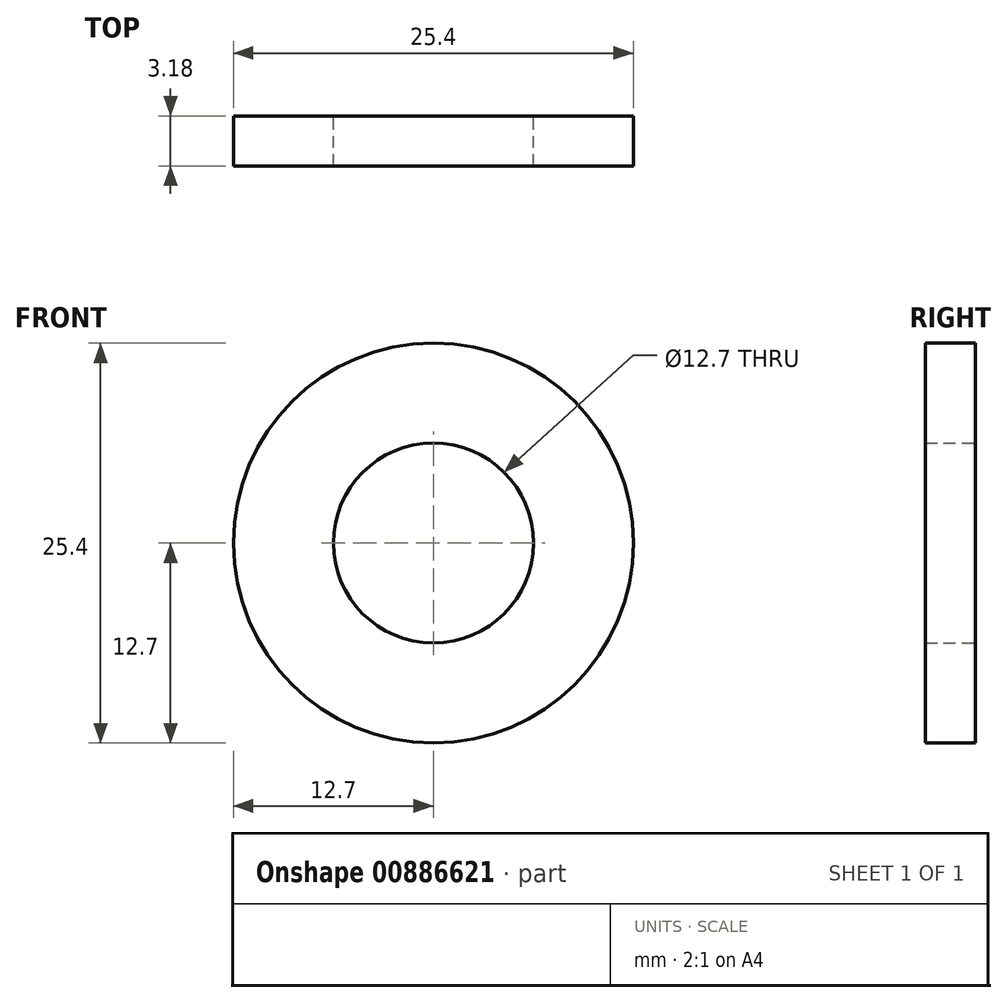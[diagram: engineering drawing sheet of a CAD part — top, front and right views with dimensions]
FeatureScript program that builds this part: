
annotation { "Feature Type Name" : "Feature", "Feature Type Description" : "" }
export const myFeature = defineFeature(function(context is Context, id is Id, definition is map)
    precondition{}
    {
        {
            assignVariable(context, id + "F0", {"name" : "thickness", "anyValue" : 3.17 * mm});
        }
        {
            var Q0;
            Q0=qCreatedBy(makeId("Front.planeOp"),FACE);
            var sketch = newSketch(context, id + "F1", { "sketchPlane" : qUnion([Q0])});
            skCircle(sketch, "E0", {"center": v(0, 0) * mm, "radius": 6.35 * mm});
            skCircle(sketch, "E1", {"center": v(0, 0) * mm, "radius": 12.7 * mm});
            skSolve(sketch);
        }
        {
            var Q0;
            Q0=makeQuery(id+"F1.imprint","IMPRINT",FACE,{"disambiguationData":[TD([[makeQuery(id+"F1.imprint","IMPRINT",EDGE,{"derivedFrom":sQuery(id+"F1.wireOp",EDGE,"E0")}),-1.0]])]});
            extrude(context, id + "F2", {"entities" : qUnion([Q0]), "depth" : getVariable(context, 'thickness'), "offsetDistance" : 25.4 * mm});
        }
    });
